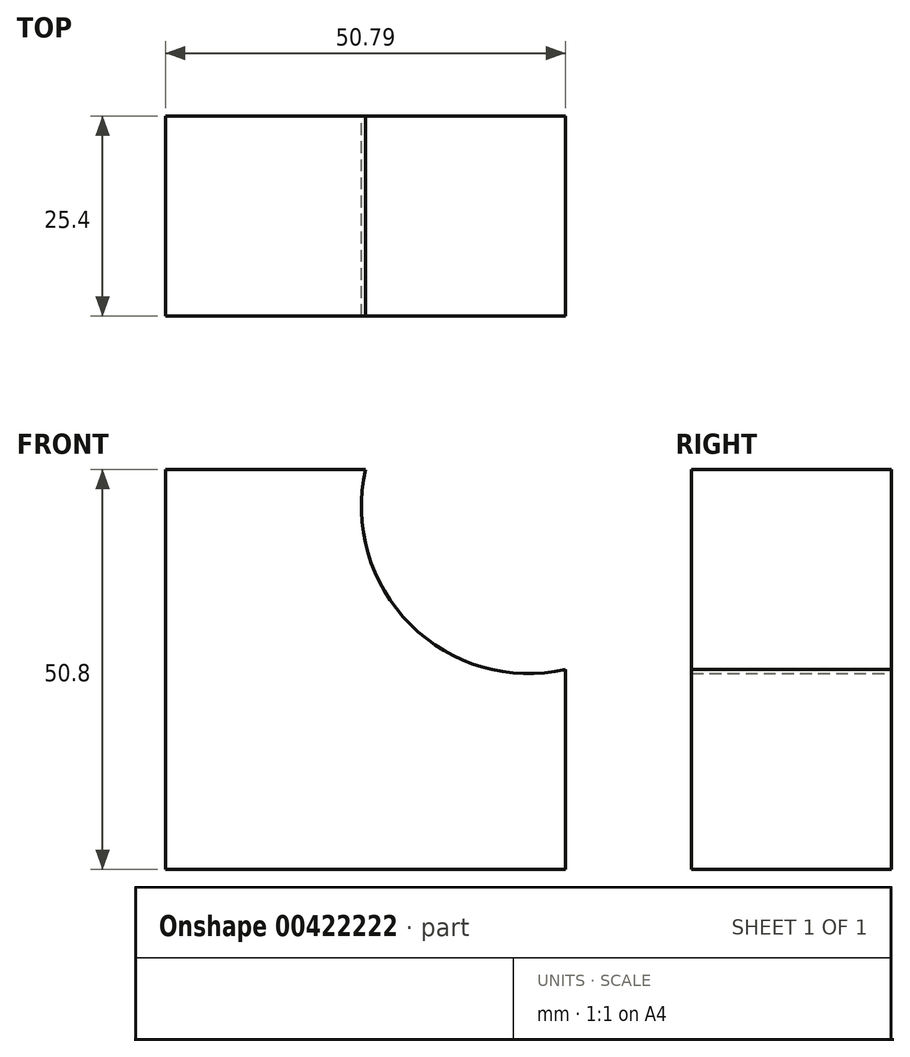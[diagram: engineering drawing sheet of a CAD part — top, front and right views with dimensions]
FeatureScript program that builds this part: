
annotation { "Feature Type Name" : "Feature", "Feature Type Description" : "" }
export const myFeature = defineFeature(function(context is Context, id is Id, definition is map)
    precondition{}
    {
        {
            var Q0;
            Q0=qCreatedBy(makeId("Front.planeOp"),FACE);
            var sketch = newSketch(context, id + "F0", { "sketchPlane" : qUnion([Q0])});
            skLineSegment(sketch, "E0", {"start": v(0, 0) * mm, "end": v(-50.8, 0) * mm});
            skLineSegment(sketch, "E1", {"start": v(-50.8, 50.8) * mm, "end": v(-50.8, 0) * mm});
            skLineSegment(sketch, "E2", {"start": v(-50.8, 50.8) * mm, "end": v(-25.4, 50.8) * mm});
            skLineSegment(sketch, "E3", {"start": v(0, 0) * mm, "end": v(0, 25.4) * mm});
            skArc(sketch, "E4", {"start": v(-25.4, 50.8) * mm, "mid": v(-19.7, 31.1) * mm, "end": v(0, 25.4) * mm});
            skSolve(sketch);
        }
        {
            var Q0;
            Q0 = qSketchRegion(id + "F0", true);
            extrude(context, id + "F1", {"entities" : qUnion([Q0]), "depth" : 25.4 * mm});
        }
    });
